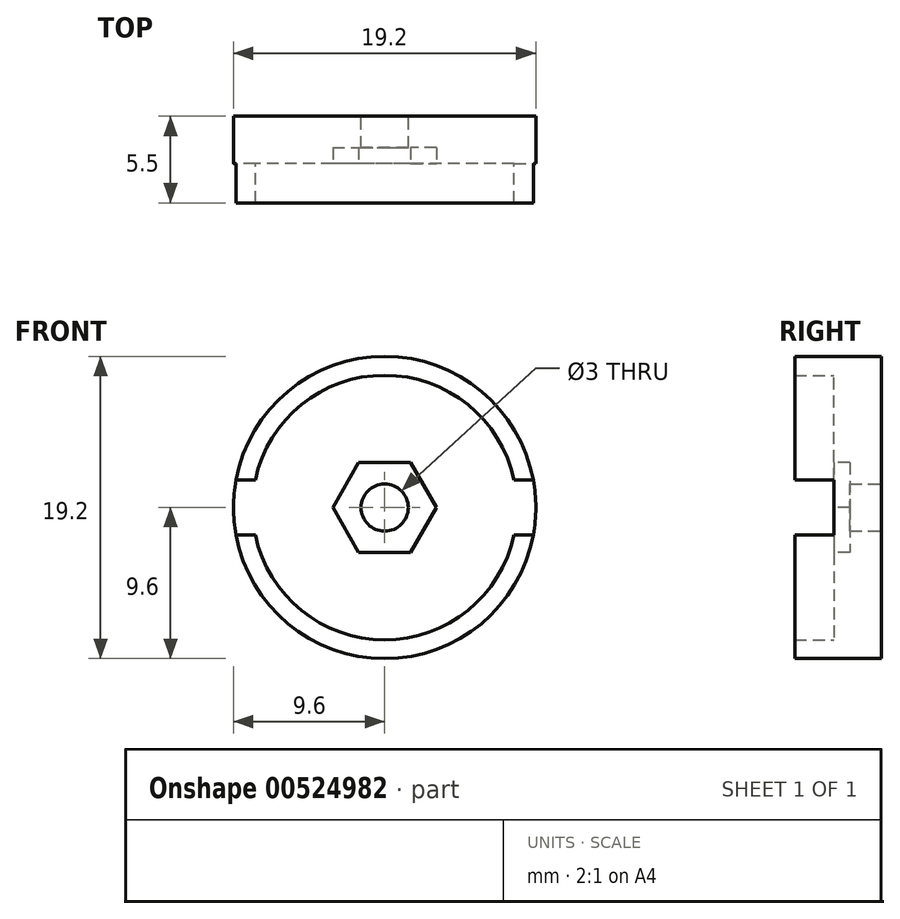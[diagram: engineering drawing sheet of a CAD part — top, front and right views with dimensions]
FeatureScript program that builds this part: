
annotation { "Feature Type Name" : "Feature", "Feature Type Description" : "" }
export const myFeature = defineFeature(function(context is Context, id is Id, definition is map)
    precondition{}
    {
        {
            var Q0;
            Q0=qCreatedBy(makeId("Front.planeOp"),FACE);
            var sketch = newSketch(context, id + "F0", { "sketchPlane" : qUnion([Q0])});
            skCircle(sketch, "E0", {"center": v(0, 0) * mm, "radius": 1.5 * mm});
            skArc(sketch, "E1", {"start": v(-9.44, -1.75) * mm, "mid": v(9.6, 0) * mm, "end": v(-9.44, 1.75) * mm});
            skLineSegment(sketch, "E2", {"start": v(-9.6, 0) * mm, "end": v(9.6, 0) * mm, "construction": true});
            skCircle(sketch, "E3", {"center": v(0, 0) * mm, "radius": 8.4 * mm});
            skLineSegment(sketch, "E4.bottom", {"start": v(-8.22, -1.75) * mm, "end": v(-9.44, -1.75) * mm});
            skLineSegment(sketch, "E4.top", {"start": v(-8.22, 1.75) * mm, "end": v(-9.44, 1.75) * mm});
            skLineSegment(sketch, "E5.bottom", {"start": v(8.22, -1.75) * mm, "end": v(9.44, -1.75) * mm});
            skLineSegment(sketch, "E5.top", {"start": v(8.22, 1.75) * mm, "end": v(9.44, 1.75) * mm});
            skArc(sketch, "E6", {"start": v(-9.44, 1.75) * mm, "mid": v(-9.6, 0) * mm, "end": v(-9.44, -1.75) * mm});
            skSolve(sketch);
        }
        {
            var Q0;
            {var subQ0=sQuery(id+"F0.wireOp",EDGE,"E4.top");Q0=makeQuery(id+"F0.imprint","IMPRINT",FACE,{"disambiguationData":[TD([[makeQuery(id+"F0.imprint","IMPRINT",EDGE,{"derivedFrom":subQ0}),-1.0]])]});}
            var Q1;
            {var subQ0=sQuery(id+"F0.wireOp",EDGE,"E4.bottom");Q1=makeQuery(id+"F0.imprint","IMPRINT",FACE,{"disambiguationData":[TD([[makeQuery(id+"F0.imprint","IMPRINT",EDGE,{"derivedFrom":subQ0}),1.0]])]});}
            extrude(context, id + "F1", {"entities" : qUnion([Q0, Q1]), "depth" : 5.5 * mm, "offsetDistance" : 25 * mm});
        }
        {
            var Q0;
            {var subQ4=sQuery(id+"F0.wireOp",EDGE,"E1");var subQ6=sQuery(id+"F0.wireOp",EDGE,"E5.top");var subQ9=makeQuery(id+"F0.imprint","INTERSECT",VERTEX,{"derivedFrom":[subQ4,subQ6]});Q0=makeQuery(id+"F0.imprint","IMPRINT",FACE,{"disambiguationData":[TD([[makeQuery(id+"F0.imprint","IMPRINT",EDGE,{"disambiguationData":[TD([[subQ9,1.0]])],"derivedFrom":subQ4}),1.0]])]});}
            var Q1;
            {var subQ1=sQuery(id+"F0.wireOp",EDGE,"E4.bottom");Q1=makeQuery(id+"F0.imprint","IMPRINT",FACE,{"disambiguationData":[TD([[makeQuery(id+"F0.imprint","IMPRINT",EDGE,{"derivedFrom":subQ1}),-1.0]])]});}
            var Q2;
            Q2=makeQuery(id+"F0.imprint","IMPRINT",FACE,{"disambiguationData":[TD([[makeQuery(id+"F0.imprint","IMPRINT",EDGE,{"derivedFrom":sQuery(id+"F0.wireOp",EDGE,"E0")}),-1.0]])]});
            extrude(context, id + "F2", {"entities" : qUnion([Q0, Q1, Q2]), "operationType" : NewBodyOperationType.ADD, "depth" : 3 * mm, "offsetDistance" : 25 * mm});
        }
        {
            var Q0;
            Q0=makeQuery(id+"F2.opExtrude","CAP_FACE",FACE,{"disambiguationData":[OSD([sQuery(id+"F0.wireOp",EDGE,"E0"),sQuery(id+"F0.wireOp",EDGE,"E3"),sQuery(id+"F0.wireOp",EDGE,"E4.left"),sQuery(id+"F0.wireOp",EDGE,"E5.left")])],"isStart":false});
            var sketch = newSketch(context, id + "F3", { "sketchPlane" : qUnion([Q0])});
            skCircle(sketch, "E7.cCircle", {"center": v(0, 0) * mm, "radius": 2.85 * mm, "construction": true});
            skLineSegment(sketch, "E7.0", {"start": v(3.3, 0) * mm, "end": v(1.65, -2.85) * mm});
            skLineSegment(sketch, "E7.1", {"start": v(1.65, -2.85) * mm, "end": v(-1.65, -2.85) * mm});
            skLineSegment(sketch, "E7.2", {"start": v(-1.65, -2.85) * mm, "end": v(-3.3, 0) * mm});
            skLineSegment(sketch, "E7.3", {"start": v(-3.3, 0) * mm, "end": v(-1.65, 2.85) * mm});
            skLineSegment(sketch, "E7.4", {"start": v(-1.65, 2.85) * mm, "end": v(1.65, 2.85) * mm});
            skLineSegment(sketch, "E7.5", {"start": v(1.65, 2.85) * mm, "end": v(3.3, 0) * mm});
            skSolve(sketch);
        }
        {
            var Q0;
            Q0=makeQuery(id+"F3.imprint","IMPRINT",FACE,{"disambiguationData":[TD([[makeQuery(id+"F3.imprint","IMPRINT",EDGE,{"derivedFrom":sQuery(id+"F3.wireOp",EDGE,"E7.0")}),-1.0]])]});
            extrude(context, id + "F4", {"entities" : qUnion([Q0]), "operationType" : NewBodyOperationType.REMOVE, "oppositeDirection" : true, "depth" : 1 * mm, "offsetDistance" : 25 * mm});
        }
    });
